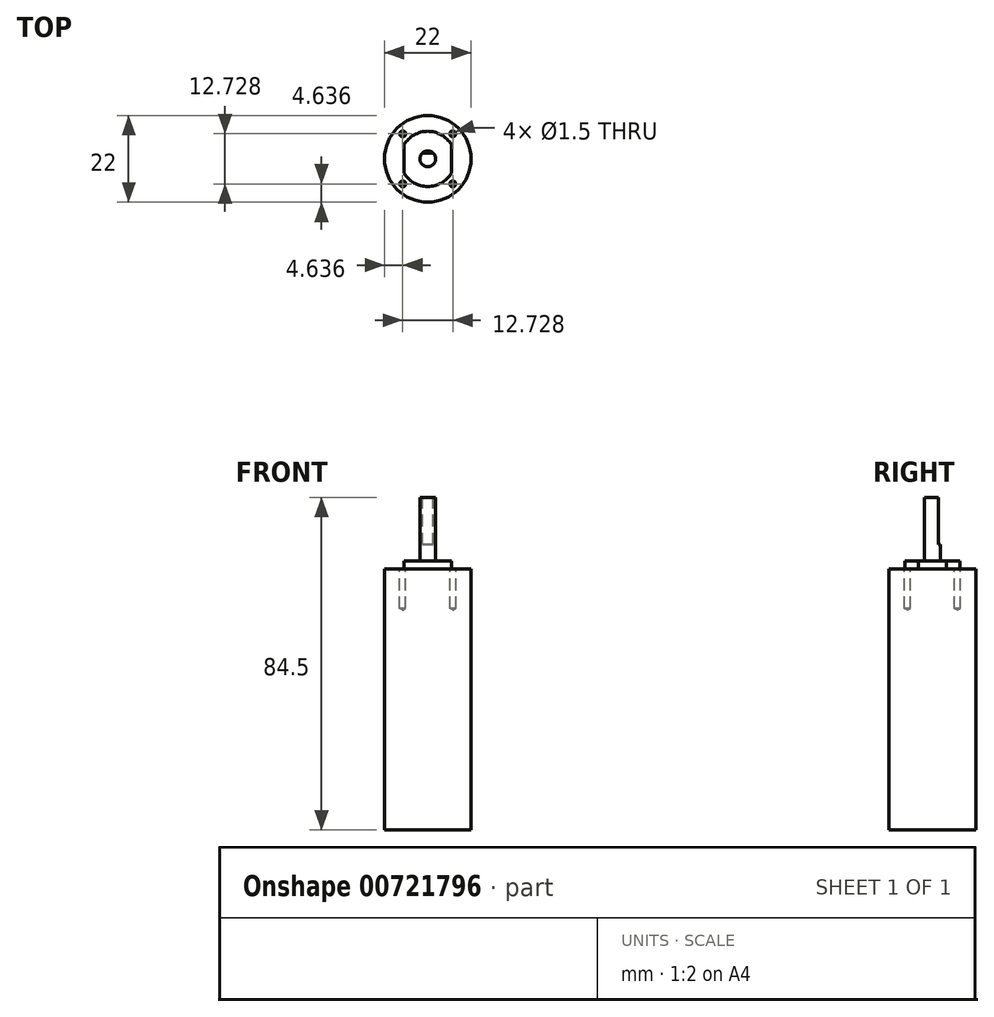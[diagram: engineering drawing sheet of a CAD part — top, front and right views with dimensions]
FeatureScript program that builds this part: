
annotation { "Feature Type Name" : "Feature", "Feature Type Description" : "" }
export const myFeature = defineFeature(function(context is Context, id is Id, definition is map)
    precondition{}
    {
        {
            var Q0;
            Q0=qCreatedBy(makeId("Top.planeOp"),FACE);
            var sketch = newSketch(context, id + "F0", { "sketchPlane" : qUnion([Q0])});
            skCircle(sketch, "E0", {"center": v(0, 0) * mm, "radius": 11 * mm});
            skSolve(sketch);
        }
        {
            var Q0;
            Q0 = qSketchRegion(id + "F0", true);
            extrude(context, id + "F1", {"entities" : qUnion([Q0]), "oppositeDirection" : true, "depth" : 66.3 * mm, "offsetDistance" : 25 * mm});
        }
        {
            var Q0;
            Q0=makeQuery(id+"F1.opExtrude","CAP_FACE",FACE,{"disambiguationData":[OSD([sQuery(id+"F0.wireOp",EDGE,"E0")])],"isStart":true});
            var sketch = newSketch(context, id + "F2", { "sketchPlane" : qUnion([Q0])});
            skCircle(sketch, "E1", {"center": v(0, 0) * mm, "radius": 7 * mm, "construction": true});
            skLineSegment(sketch, "E2.bottom", {"start": v(-6, 3.6) * mm, "end": v(6, 3.6) * mm, "construction": true});
            skLineSegment(sketch, "E2.top", {"start": v(-6, -3.6) * mm, "end": v(6, -3.6) * mm, "construction": true});
            skLineSegment(sketch, "E2.left", {"start": v(-6, 3.6) * mm, "end": v(-6, -3.6) * mm});
            skLineSegment(sketch, "E2.right", {"start": v(6, 3.6) * mm, "end": v(6, -3.6) * mm});
            skArc(sketch, "E3", {"start": v(-6, 3.6) * mm, "mid": v(0, 7) * mm, "end": v(6, 3.6) * mm});
            skArc(sketch, "E4", {"start": v(-6, -3.6) * mm, "mid": v(0, -7) * mm, "end": v(6, -3.6) * mm});
            skSolve(sketch);
        }
        {
            var Q0;
            Q0 = qSketchRegion(id + "F2", true);
            extrude(context, id + "F3", {"entities" : qUnion([Q0]), "operationType" : NewBodyOperationType.ADD, "depth" : 2 * mm, "offsetDistance" : 25 * mm});
        }
        {
            var Q0;
            Q0=makeQuery(id+"F3.opExtrude","CAP_FACE",FACE,{"disambiguationData":[OSD([sQuery(id+"F2.wireOp",EDGE,"E2.left"),sQuery(id+"F2.wireOp",EDGE,"E2.right"),sQuery(id+"F2.wireOp",EDGE,"E3"),sQuery(id+"F2.wireOp",EDGE,"E4")])],"isStart":false});
            var sketch = newSketch(context, id + "F4", { "sketchPlane" : qUnion([Q0])});
            skCircle(sketch, "E5", {"center": v(0, 0) * mm, "radius": 2 * mm});
            skSolve(sketch);
        }
        {
            var Q0;
            Q0 = qSketchRegion(id + "F4", true);
            extrude(context, id + "F5", {"entities" : qUnion([Q0]), "operationType" : NewBodyOperationType.ADD, "depth" : (18.2 - 2) * mm, "offsetDistance" : 25 * mm});
        }
        {
            var Q0;
            Q0=makeQuery(id+"F5.opExtrude","CAP_FACE",FACE,{"disambiguationData":[OSD([sQuery(id+"F4.wireOp",EDGE,"E5")])],"isStart":false});
            var sketch = newSketch(context, id + "F6", { "sketchPlane" : qUnion([Q0])});
            skLineSegment(sketch, "E6.bottom", {"start": v(-1.32, 1.5) * mm, "end": v(1.32, 1.5) * mm});
            skLineSegment(sketch, "E6.top", {"start": v(-1.32, 2) * mm, "end": v(1.32, 2) * mm});
            skLineSegment(sketch, "E6.left", {"start": v(-1.32, 1.5) * mm, "end": v(-1.32, 2) * mm});
            skLineSegment(sketch, "E6.right", {"start": v(1.32, 1.5) * mm, "end": v(1.32, 2) * mm});
            skCircle(sketch, "E7.0", {"center": v(0, 0) * mm, "radius": 2 * mm, "construction": true});
            skSolve(sketch);
        }
        {
            var Q0;
            Q0 = qSketchRegion(id + "F6", true);
            extrude(context, id + "F7", {"entities" : qUnion([Q0]), "operationType" : NewBodyOperationType.REMOVE, "oppositeDirection" : true, "depth" : 12 * mm, "offsetDistance" : 25 * mm});
        }
        {
            var Q0;
            Q0=makeQuery(id+"F1.opExtrude","CAP_FACE",FACE,{"disambiguationData":[OSD([sQuery(id+"F0.wireOp",EDGE,"E0")])],"isStart":true});
            var sketch = newSketch(context, id + "F8", { "sketchPlane" : qUnion([Q0])});
            skLineSegment(sketch, "E8.bottom", {"start": v(-6.36, 6.36) * mm, "end": v(6.36, 6.36) * mm, "construction": true});
            skLineSegment(sketch, "E8.top", {"start": v(-6.36, -6.36) * mm, "end": v(6.36, -6.36) * mm, "construction": true});
            skLineSegment(sketch, "E8.left", {"start": v(-6.36, 6.36) * mm, "end": v(-6.36, -6.36) * mm, "construction": true});
            skLineSegment(sketch, "E8.right", {"start": v(6.36, 6.36) * mm, "end": v(6.36, -6.36) * mm, "construction": true});
            skCircle(sketch, "E9", {"center": v(0, 0) * mm, "radius": 9 * mm, "construction": true});
            skPoint(sketch, "E10", {"position": v(-6.36, 6.36) * mm});
            skPoint(sketch, "E11", {"position": v(6.36, 6.36) * mm});
            skPoint(sketch, "E12", {"position": v(6.36, -6.36) * mm});
            skPoint(sketch, "E13", {"position": v(-6.36, -6.36) * mm});
            skSolve(sketch);
        }
        {
            var Q0;
            Q0=sQuery(id+"F8.wireOp",VERTEX,"E10");
            var Q1;
            Q1=sQuery(id+"F8.wireOp",VERTEX,"E13");
            var Q2;
            Q2=sQuery(id+"F8.wireOp",VERTEX,"E11");
            var Q3;
            Q3=sQuery(id+"F8.wireOp",VERTEX,"E12");
            var Q4;
            Q4=makeQuery(id+"F1.opExtrude","SWEPT_BODY",BODY,{"disambiguationData":[OSD([sQuery(id+"F0.wireOp",EDGE,"E0")])]});
            hole(context, id + "F9", {"style" : HoleStyle.SIMPLE, "endStyle" : HoleEndStyle.BLIND, "holeDiameter" : 1.5 * mm, "majorDiameter" : 3 * mm, "holeDepth" : 10 * mm, "isTappedThrough" : true, "tappedDepth" : 12 * mm, "tapClearance" : 3, "startFromSketch" : true, "locations" : qUnion([Q0, Q1, Q2, Q3]), "scope" : qUnion([Q4])});
        }
    });
